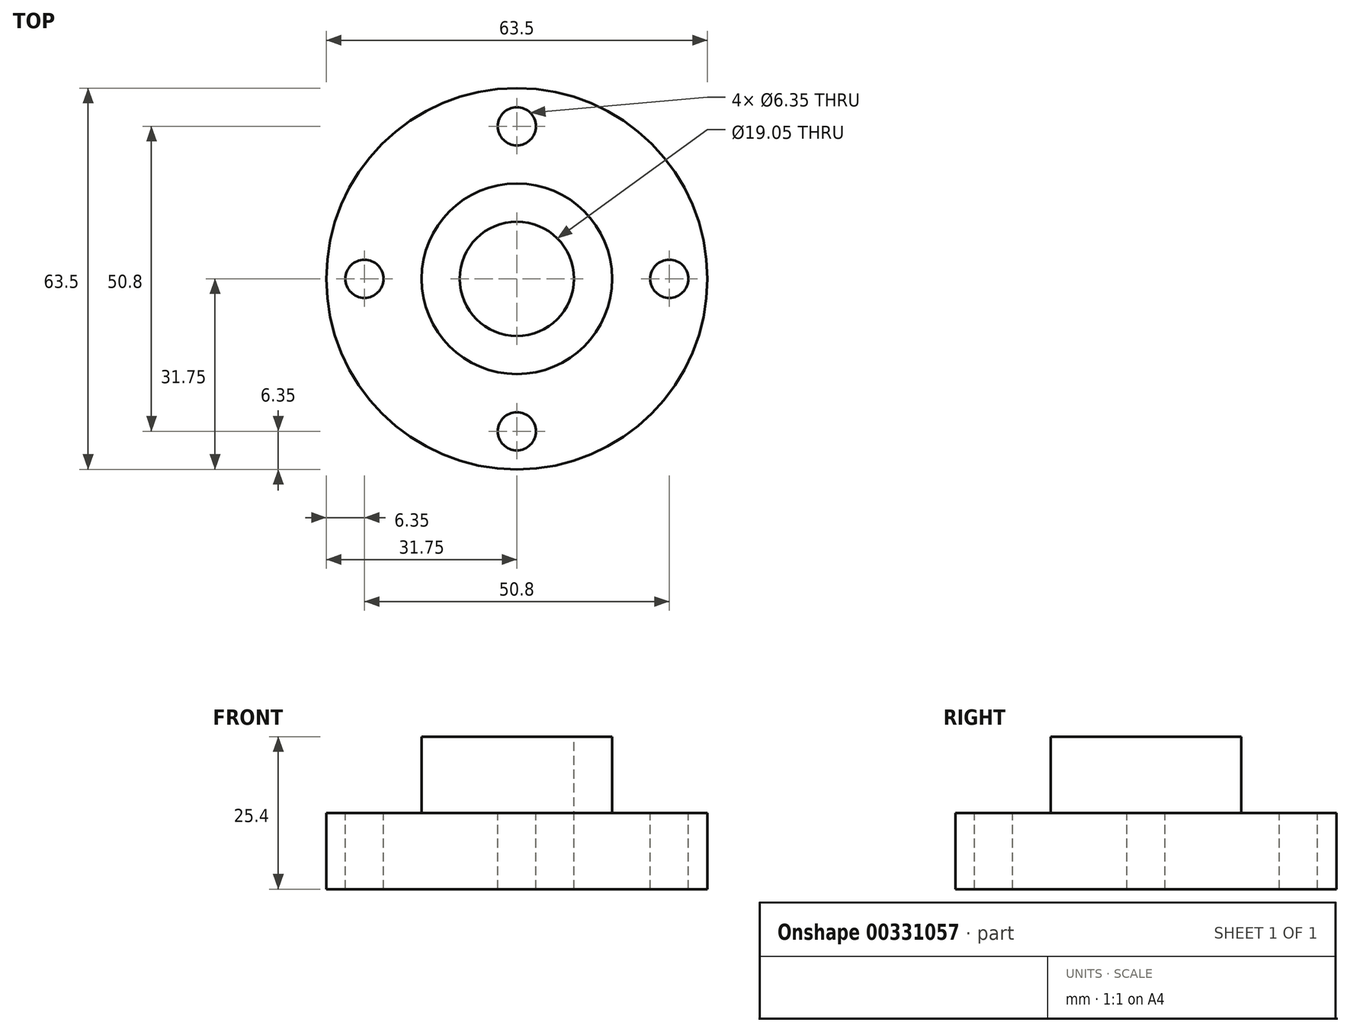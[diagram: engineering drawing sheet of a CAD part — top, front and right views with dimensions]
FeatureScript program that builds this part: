
annotation { "Feature Type Name" : "Feature", "Feature Type Description" : "" }
export const myFeature = defineFeature(function(context is Context, id is Id, definition is map)
    precondition{}
    {
        {
            var Q0;
            Q0=qCreatedBy(makeId("Top.planeOp"),FACE);
            var sketch = newSketch(context, id + "F0", { "sketchPlane" : qUnion([Q0])});
            skCircle(sketch, "E0", {"center": v(0, 0) * mm, "radius": 31.75 * mm});
            skSolve(sketch);
        }
        {
            var Q0;
            Q0 = qSketchRegion(id + "F0", true);
            extrude(context, id + "F1", {"entities" : qUnion([Q0]), "depth" : 12.7 * mm});
        }
        {
            var Q0;
            Q0=makeQuery(id+"F1.opExtrude","CAP_FACE",FACE,{"disambiguationData":[OSD([sQuery(id+"F0.wireOp",EDGE,"E0")])],"isStart":false});
            var sketch = newSketch(context, id + "F2", { "sketchPlane" : qUnion([Q0])});
            skPoint(sketch, "E1.0", {"position": v(0, 0) * mm});
            skCircle(sketch, "E2", {"center": v(0, 0) * mm, "radius": 15.88 * mm});
            skSolve(sketch);
        }
        {
            var Q0;
            Q0 = qSketchRegion(id + "F2", true);
            extrude(context, id + "F3", {"entities" : qUnion([Q0]), "operationType" : NewBodyOperationType.ADD, "depth" : 12.7 * mm});
        }
        {
            var Q0;
            Q0=makeQuery(id+"F3.opExtrude","CAP_FACE",FACE,{"disambiguationData":[OSD([sQuery(id+"F2.wireOp",EDGE,"E2")])],"isStart":false});
            var sketch = newSketch(context, id + "F4", { "sketchPlane" : qUnion([Q0])});
            skPoint(sketch, "E3.0", {"position": v(0, 0) * mm});
            skCircle(sketch, "E4", {"center": v(0, 0) * mm, "radius": 9.53 * mm});
            skSolve(sketch);
        }
        {
            var Q0;
            Q0 = qSketchRegion(id + "F4", true);
            extrude(context, id + "F5", {"entities" : qUnion([Q0]), "operationType" : NewBodyOperationType.REMOVE, "endBound" : BoundingType.THROUGH_ALL, "oppositeDirection" : true, "depth" : 25.4 * mm});
        }
        {
            var Q0;
            Q0=makeQuery(id+"F1.opExtrude","CAP_FACE",FACE,{"disambiguationData":[OSD([sQuery(id+"F0.wireOp",EDGE,"E0")])],"isStart":false});
            var sketch = newSketch(context, id + "F6", { "sketchPlane" : qUnion([Q0])});
            skPoint(sketch, "E5.0", {"position": v(0, 0) * mm});
            skCircle(sketch, "E6", {"center": v(0, 25.4) * mm, "radius": 3.18 * mm});
            skCircle(sketch, "E7", {"center": v(25.4, 0) * mm, "radius": 3.18 * mm});
            skCircle(sketch, "E8", {"center": v(0, -25.4) * mm, "radius": 3.18 * mm});
            skCircle(sketch, "E9", {"center": v(-25.4, 0) * mm, "radius": 3.18 * mm});
            skSolve(sketch);
        }
        {
            var Q0;
            Q0 = qSketchRegion(id + "F6", true);
            extrude(context, id + "F7", {"entities" : qUnion([Q0]), "operationType" : NewBodyOperationType.REMOVE, "oppositeDirection" : true, "depth" : 25.4 * mm});
        }
    });
